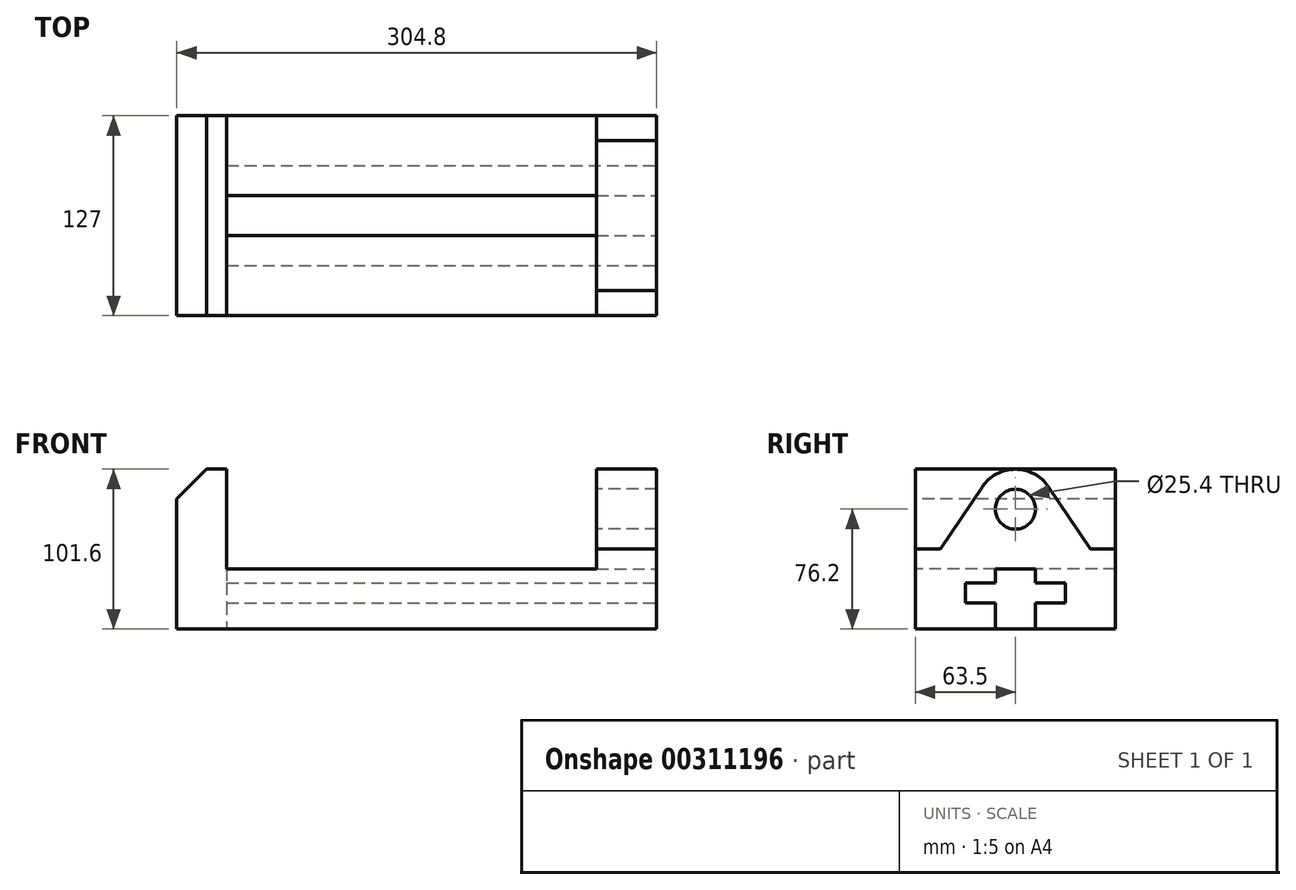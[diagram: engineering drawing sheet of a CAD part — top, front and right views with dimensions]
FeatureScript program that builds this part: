
annotation { "Feature Type Name" : "Feature", "Feature Type Description" : "" }
export const myFeature = defineFeature(function(context is Context, id is Id, definition is map)
    precondition{}
    {
        {
            var Q0;
            Q0=qCreatedBy(makeId("Right.planeOp"),FACE);
            var sketch = newSketch(context, id + "F0", { "sketchPlane" : qUnion([Q0])});
            skLineSegment(sketch, "E0", {"start": v(0, 0) * mm, "end": v(127, 0) * mm});
            skLineSegment(sketch, "E1", {"start": v(127, 0) * mm, "end": v(127, 50.8) * mm});
            skLineSegment(sketch, "E2", {"start": v(127, 50.8) * mm, "end": v(111.12, 50.8) * mm});
            skLineSegment(sketch, "E3", {"start": v(111.12, 50.8) * mm, "end": v(84.6, 90.35) * mm});
            skLineSegment(sketch, "E4", {"start": v(0, 0) * mm, "end": v(0, 50.8) * mm});
            skLineSegment(sketch, "E5", {"start": v(0, 50.8) * mm, "end": v(15.88, 50.8) * mm});
            skLineSegment(sketch, "E6", {"start": v(15.88, 50.8) * mm, "end": v(42.4, 90.35) * mm});
            skArc(sketch, "E7", {"start": v(84.6, 90.35) * mm, "mid": v(63.5, 101.6) * mm, "end": v(42.4, 90.35) * mm});
            skCircle(sketch, "E8", {"center": v(63.5, 76.2) * mm, "radius": 12.7 * mm});
            skSolve(sketch);
        }
        {
            var Q0;
            Q0 = qSketchRegion(id + "F0", true);
            var Q1;
            Q1 = qSketchRegion(id + "F2", true);
            extrude(context, id + "F1", {"entities" : qUnion([Q0, Q1]), "depth" : 38.1 * mm});
        }
        {
            var Q0;
            Q0=makeQuery(id+"F1.opExtrude","SWEPT_FACE",FACE,{"disambiguationData":[OSD([sQuery(id+"F0.wireOp",EDGE,"E4")])]});
            var sketch = newSketch(context, id + "F2", { "sketchPlane" : qUnion([Q0])});
            skLineSegment(sketch, "E9", {"start": v(0, 38.1) * mm, "end": v(0, 0) * mm});
            skLineSegment(sketch, "E10", {"start": v(0, 0) * mm, "end": v(-266.7, 0) * mm});
            skLineSegment(sketch, "E11", {"start": v(-266.7, 0) * mm, "end": v(-266.7, 82.55) * mm});
            skLineSegment(sketch, "E12", {"start": v(-266.7, 82.55) * mm, "end": v(-247.65, 101.6) * mm});
            skLineSegment(sketch, "E13", {"start": v(-247.65, 101.6) * mm, "end": v(-234.95, 101.6) * mm});
            skLineSegment(sketch, "E14", {"start": v(-234.95, 101.6) * mm, "end": v(-234.95, 38.1) * mm});
            skLineSegment(sketch, "E15", {"start": v(-234.95, 38.1) * mm, "end": v(0, 38.1) * mm});
            skSolve(sketch);
        }
        {
            var Q0;
            Q0 = qSketchRegion(id + "F2", true);
            extrude(context, id + "F3", {"entities" : qUnion([Q0]), "operationType" : NewBodyOperationType.ADD, "oppositeDirection" : true, "depth" : 127 * mm});
        }
        {
            var Q0;
            Q0=makeQuery(id+"F1.opExtrude","CAP_FACE",FACE,{"disambiguationData":[OSD([sQuery(id+"F0.wireOp",EDGE,"E0"),sQuery(id+"F0.wireOp",EDGE,"E1"),sQuery(id+"F0.wireOp",EDGE,"E2"),sQuery(id+"F0.wireOp",EDGE,"E3"),sQuery(id+"F0.wireOp",EDGE,"E4"),sQuery(id+"F0.wireOp",EDGE,"E5"),sQuery(id+"F0.wireOp",EDGE,"E6"),sQuery(id+"F0.wireOp",EDGE,"E7"),sQuery(id+"F0.wireOp",EDGE,"E8")])],"isStart":false});
            var sketch = newSketch(context, id + "F4", { "sketchPlane" : qUnion([Q0])});
            skLineSegment(sketch, "E16", {"start": v(63.5, 0) * mm, "end": v(50.8, 0) * mm});
            skLineSegment(sketch, "E17", {"start": v(63.5, 0) * mm, "end": v(76.2, 0) * mm});
            skLineSegment(sketch, "E18", {"start": v(76.2, 0) * mm, "end": v(76.2, 16.51) * mm});
            skLineSegment(sketch, "E19", {"start": v(76.2, 16.51) * mm, "end": v(95.25, 16.51) * mm});
            skLineSegment(sketch, "E20", {"start": v(95.25, 16.51) * mm, "end": v(95.25, 29.21) * mm});
            skLineSegment(sketch, "E21", {"start": v(95.25, 29.21) * mm, "end": v(76.2, 29.21) * mm});
            skLineSegment(sketch, "E22", {"start": v(76.2, 29.21) * mm, "end": v(76.2, 38.1) * mm});
            skLineSegment(sketch, "E23", {"start": v(76.2, 38.1) * mm, "end": v(50.8, 38.1) * mm});
            skLineSegment(sketch, "E24", {"start": v(50.8, 38.1) * mm, "end": v(50.8, 29.21) * mm});
            skLineSegment(sketch, "E25", {"start": v(50.8, 29.21) * mm, "end": v(31.75, 29.21) * mm});
            skLineSegment(sketch, "E26", {"start": v(31.75, 29.21) * mm, "end": v(31.75, 16.51) * mm});
            skLineSegment(sketch, "E27", {"start": v(31.75, 16.51) * mm, "end": v(50.8, 16.51) * mm});
            skLineSegment(sketch, "E28", {"start": v(50.8, 16.51) * mm, "end": v(50.8, 0) * mm});
            skSolve(sketch);
        }
        {
            var Q0;
            Q0 = qSketchRegion(id + "F4", true);
            extrude(context, id + "F5", {"entities" : qUnion([Q0]), "operationType" : NewBodyOperationType.REMOVE, "oppositeDirection" : true, "depth" : 273.05 * mm});
        }
    });
